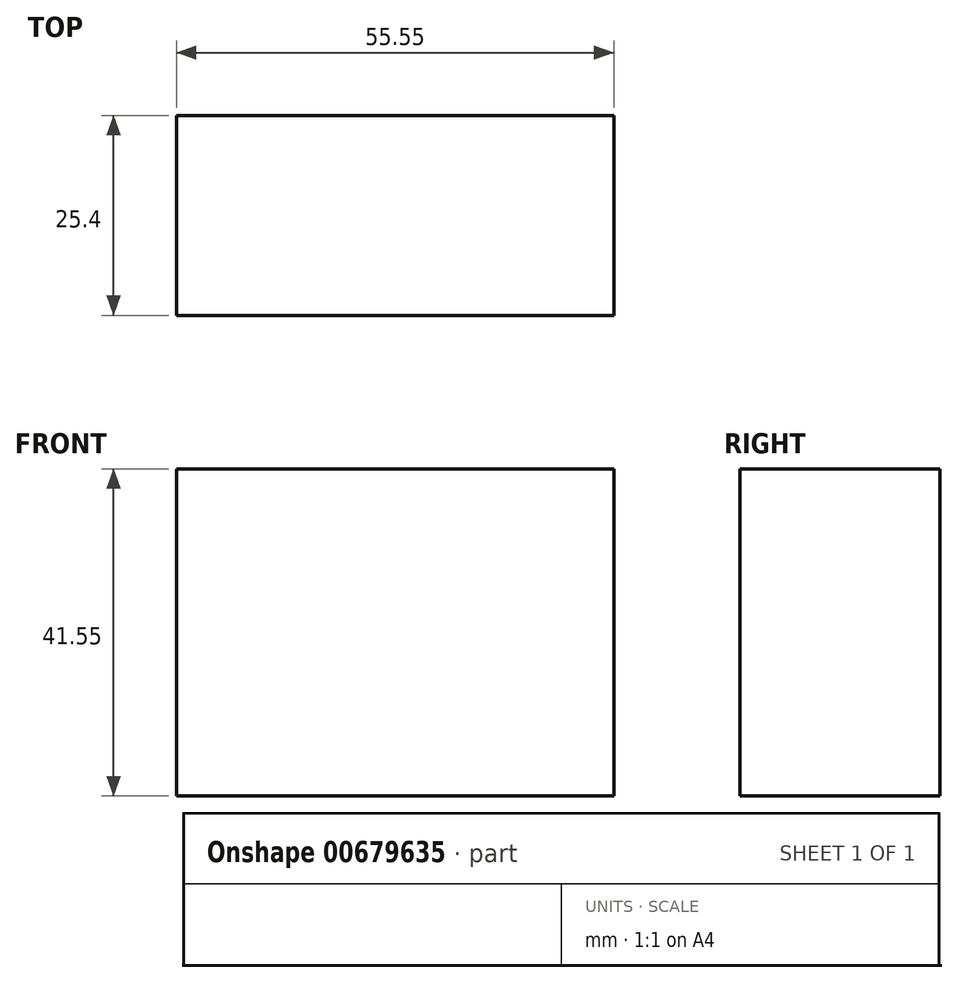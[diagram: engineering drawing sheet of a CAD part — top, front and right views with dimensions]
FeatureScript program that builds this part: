
annotation { "Feature Type Name" : "Feature", "Feature Type Description" : "" }
export const myFeature = defineFeature(function(context is Context, id is Id, definition is map)
    precondition{}
    {
        {
            var Q0;
            Q0=qCreatedBy(makeId("Front.planeOp"),FACE);
            var sketch = newSketch(context, id + "F0", { "sketchPlane" : qUnion([Q0])});
            skLineSegment(sketch, "E0.bottom", {"start": v(-85.87, 63.62) * mm, "end": v(-30.32, 63.62) * mm});
            skLineSegment(sketch, "E0.top", {"start": v(-85.87, 22.07) * mm, "end": v(-30.32, 22.07) * mm});
            skLineSegment(sketch, "E0.left", {"start": v(-85.87, 63.62) * mm, "end": v(-85.87, 22.07) * mm});
            skLineSegment(sketch, "E0.right", {"start": v(-30.32, 63.62) * mm, "end": v(-30.32, 22.07) * mm});
            skSolve(sketch);
        }
        {
            var Q0;
            Q0 = qSketchRegion(id + "F0", true);
            extrude(context, id + "F1", {"entities" : qUnion([Q0]), "depth" : 25.4 * mm, "offsetDistance" : 25.4 * mm});
        }
    });
